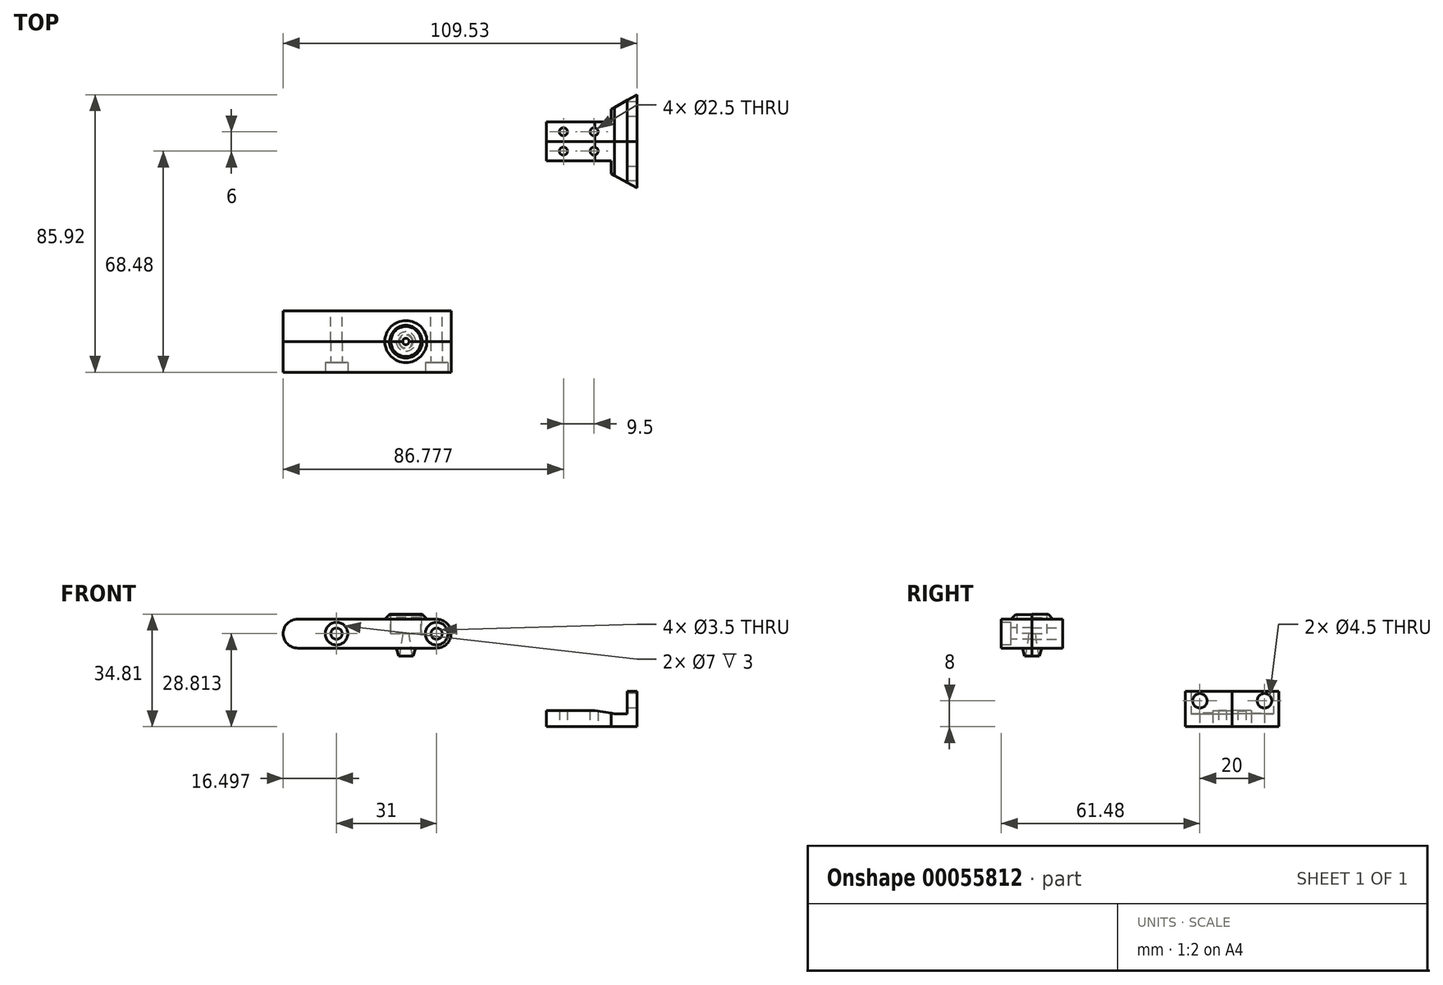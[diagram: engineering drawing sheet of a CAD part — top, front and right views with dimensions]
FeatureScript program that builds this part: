
annotation { "Feature Type Name" : "Feature", "Feature Type Description" : "" }
export const myFeature = defineFeature(function(context is Context, id is Id, definition is map)
    precondition{}
    {
        {
            var Q0;
            Q0=qCreatedBy(makeId("Front.planeOp"),FACE);
            var sketch = newSketch(context, id + "F0", { "sketchPlane" : qUnion([Q0])});
            skLineSegment(sketch, "E0.bottom", {"start": v(-22.8, 33.31) * mm, "end": v(29.2, 33.31) * mm});
            skLineSegment(sketch, "E0.top", {"start": v(-22.8, 24.31) * mm, "end": v(29.2, 24.31) * mm});
            skLineSegment(sketch, "E0.left", {"start": v(-22.8, 33.31) * mm, "end": v(-22.8, 24.31) * mm});
            skLineSegment(sketch, "E0.right", {"start": v(29.2, 33.31) * mm, "end": v(29.2, 24.31) * mm});
            skSolve(sketch);
        }
        {
            var Q0;
            Q0=makeQuery(id+"F0.imprint","IMPRINT",FACE,{"disambiguationData":[TD([[makeQuery(id+"F0.imprint","IMPRINT",EDGE,{"derivedFrom":sQuery(id+"F0.wireOp",EDGE,"E0.bottom")}),-1.0]])]});
            extrude(context, id + "F1", {"entities" : qUnion([Q0]), "depth" : 9.5 * mm});
        }
        {
            var Q0;
            Q0=makeQuery(id+"F1.opExtrude","SWEPT_FACE",FACE,{"disambiguationData":[OSD([sQuery(id+"F0.wireOp",EDGE,"E0.bottom")])]});
            var sketch = newSketch(context, id + "F2", { "sketchPlane" : qUnion([Q0])});
            skCircle(sketch, "E1", {"center": v(15.2, -9.5) * mm, "radius": 4.65 * mm});
            skCircle(sketch, "E2", {"center": v(15.2, -9.5) * mm, "radius": 6.5 * mm});
            skSolve(sketch);
        }
        {
            var Q0;
            {var subQ0=sQuery(id+"F2.wireOp",EDGE,"E1");var subQ1=makeQuery(id+"F1.opExtrude","CAP_EDGE",EDGE,{"disambiguationData":[OSD([sQuery(id+"F0.wireOp",EDGE,"E0.bottom")])],"isStart":false});var subQ2=makeQuery(id+"F2.imprint","INTERSECT",VERTEX,{"disambiguationData":[OD(0.0)],"derivedFrom":[subQ1,subQ0]});Q0=makeQuery(id+"F2.imprint","IMPRINT",FACE,{"disambiguationData":[TD([[makeQuery(id+"F2.imprint","IMPRINT",EDGE,{"disambiguationData":[TD([[subQ2,1.0]])],"derivedFrom":subQ0}),1.0]])]});}
            extrude(context, id + "F3", {"entities" : qUnion([Q0]), "operationType" : NewBodyOperationType.REMOVE, "oppositeDirection" : true, "depth" : 4.5 * mm});
        }
        {
            var Q0;
            {var subQ0=sQuery(id+"F2.wireOp",EDGE,"E1");var subQ1=makeQuery(id+"F1.opExtrude","CAP_EDGE",EDGE,{"disambiguationData":[OSD([sQuery(id+"F0.wireOp",EDGE,"E0.bottom")])],"isStart":false});var subQ2=makeQuery(id+"F2.imprint","INTERSECT",VERTEX,{"disambiguationData":[OD(0.0)],"derivedFrom":[subQ1,subQ0]});Q0=makeQuery(id+"F2.imprint","IMPRINT",FACE,{"disambiguationData":[TD([[makeQuery(id+"F2.imprint","IMPRINT",EDGE,{"disambiguationData":[TD([[subQ2,1.0]])],"derivedFrom":subQ0}),-1.0]])]});}
            var Q1;
            Q1=sQuery(id+"F2.wireOp",EDGE,"E1");
            var Q2;
            Q2=sQuery(id+"F2.wireOp",EDGE,"E2");
            extrude(context, id + "F4", {"entities" : qUnion([Q0]), "operationType" : NewBodyOperationType.ADD, "surfaceEntities" : qUnion([Q1, Q2]), "depth" : 1.5 * mm});
        }
        {
            var Q0;
            Q0=makeQuery(id+"F4.opExtrude","CAP_EDGE",EDGE,{"disambiguationData":[OSD([sQuery(id+"F2.wireOp",EDGE,"E2")])],"isStart":false});
            chamfer(context, id + "F5", {"entities" : qUnion([Q0]), "width" : 1.5 * mm});
        }
        {
            var Q0;
            {var subQ0=sQuery(id+"F2.wireOp",EDGE,"E2");var subQ1=sQuery(id+"F0.wireOp",EDGE,"E0.bottom");var subQ2=makeQuery(id+"F1.opExtrude","CAP_EDGE",EDGE,{"disambiguationData":[OSD([subQ1])],"isStart":false});Q0=makeQuery(id+"F4.boolean.opBoolean","MERGE",FACE,{"derivedFrom":[makeQuery(id+"F1.opExtrude","CAP_FACE",FACE,{"disambiguationData":[OSD([subQ1,sQuery(id+"F0.wireOp",EDGE,"E0.top"),sQuery(id+"F0.wireOp",EDGE,"E0.left"),sQuery(id+"F0.wireOp",EDGE,"E0.right")])],"isStart":false}),makeQuery(id+"F4.opExtrude","SWEPT_FACE",FACE,{"disambiguationData":[OSD([subQ1]),TDD([makeQuery(id+"F2.imprint","IMPRINT",EDGE,{"disambiguationData":[TD([[makeQuery(id+"F2.imprint","INTERSECT",VERTEX,{"disambiguationData":[OD(0.0)],"derivedFrom":[subQ2,subQ0]}),-1.0]])],"derivedFrom":subQ2})])]}),makeQuery(id+"F4.opExtrude","SWEPT_FACE",FACE,{"disambiguationData":[OSD([subQ1]),TDD([makeQuery(id+"F2.imprint","IMPRINT",EDGE,{"disambiguationData":[TD([[makeQuery(id+"F2.imprint","INTERSECT",VERTEX,{"disambiguationData":[OD(1.0)],"derivedFrom":[subQ2,subQ0]}),1.0]])],"derivedFrom":subQ2})])]})]});}
            var sketch = newSketch(context, id + "F6", { "sketchPlane" : qUnion([Q0])});
            skLineSegment(sketch, "E3", {"start": v(15.2, 28.81) * mm, "end": v(15.2, 21.81) * mm});
            skLineSegment(sketch, "E4", {"start": v(15.2, 21.81) * mm, "end": v(18.2, 21.81) * mm});
            skLineSegment(sketch, "E5", {"start": v(18.2, 21.81) * mm, "end": v(18.2, 24.31) * mm});
            skLineSegment(sketch, "E6", {"start": v(18.2, 24.31) * mm, "end": v(16.2, 28.81) * mm});
            skLineSegment(sketch, "E7", {"start": v(16.2, 28.81) * mm, "end": v(15.2, 28.81) * mm});
            skSolve(sketch);
        }
        {
            var Q0;
            {var subQ0=sQuery(id+"F6.wireOp",EDGE,"E4");Q0=makeQuery(id+"F6.imprint","IMPRINT",FACE,{"disambiguationData":[TD([[makeQuery(id+"F6.imprint","IMPRINT",EDGE,{"derivedFrom":subQ0}),1.0]])]});}
            var Q1;
            {var subQ4=sQuery(id+"F6.wireOp",EDGE,"E6");Q1=makeQuery(id+"F6.imprint","IMPRINT",FACE,{"disambiguationData":[TD([[makeQuery(id+"F6.imprint","IMPRINT",EDGE,{"derivedFrom":subQ4}),1.0]])]});}
            var Q2;
            Q2=sQuery(id+"F6.wireOp",EDGE,"E3");
            revolve(context, id + "F7", {"operationType" : NewBodyOperationType.ADD, "entities" : qUnion([Q0, Q1]), "axis" : qUnion([Q2]), "revolveType" : RevolveType.ONE_DIRECTION, "oppositeDirection" : true, "angle" : 180 * degree});
        }
        {
            var Q0;
            {var subQ0=sQuery(id+"F2.wireOp",EDGE,"E2");var subQ1=sQuery(id+"F0.wireOp",EDGE,"E0.bottom");var subQ2=makeQuery(id+"F1.opExtrude","CAP_EDGE",EDGE,{"disambiguationData":[OSD([subQ1])],"isStart":false});Q0=makeQuery(id+"F7.boolean.opBoolean","MERGE",FACE,{"derivedFrom":[makeQuery(id+"F4.boolean.opBoolean","MERGE",FACE,{"derivedFrom":[makeQuery(id+"F1.opExtrude","CAP_FACE",FACE,{"disambiguationData":[OSD([subQ1,sQuery(id+"F0.wireOp",EDGE,"E0.top"),sQuery(id+"F0.wireOp",EDGE,"E0.left"),sQuery(id+"F0.wireOp",EDGE,"E0.right")])],"isStart":false}),makeQuery(id+"F4.opExtrude","SWEPT_FACE",FACE,{"disambiguationData":[OSD([subQ1]),TDD([makeQuery(id+"F2.imprint","IMPRINT",EDGE,{"disambiguationData":[TD([[makeQuery(id+"F2.imprint","INTERSECT",VERTEX,{"disambiguationData":[OD(0.0)],"derivedFrom":[subQ2,subQ0]}),-1.0]])],"derivedFrom":subQ2})])]}),makeQuery(id+"F4.opExtrude","SWEPT_FACE",FACE,{"disambiguationData":[OSD([subQ1]),TDD([makeQuery(id+"F2.imprint","IMPRINT",EDGE,{"disambiguationData":[TD([[makeQuery(id+"F2.imprint","INTERSECT",VERTEX,{"disambiguationData":[OD(1.0)],"derivedFrom":[subQ2,subQ0]}),1.0]])],"derivedFrom":subQ2})])]})]}),makeQuery(id+"F7.opRevolve","CAP_FACE",FACE,{"disambiguationData":[OSD([sQuery(id+"F6.wireOp",EDGE,"E3"),sQuery(id+"F6.wireOp",EDGE,"E4"),sQuery(id+"F6.wireOp",EDGE,"E5"),sQuery(id+"F6.wireOp",EDGE,"E6"),sQuery(id+"F6.wireOp",EDGE,"E7")])],"isStart":false})]});}
            var sketch = newSketch(context, id + "F8", { "sketchPlane" : qUnion([Q0])});
            skLineSegment(sketch, "E8", {"start": v(15.2, 28.81) * mm, "end": v(15.2, 21.81) * mm});
            skLineSegment(sketch, "E9", {"start": v(15.2, 21.81) * mm, "end": v(17.2, 21.81) * mm});
            skLineSegment(sketch, "E10", {"start": v(17.2, 21.81) * mm, "end": v(16.2, 28.81) * mm});
            skLineSegment(sketch, "E11", {"start": v(16.2, 28.81) * mm, "end": v(15.2, 28.81) * mm});
            skSolve(sketch);
        }
        {
            var Q0;
            Q0=makeQuery(id+"F8.imprint","IMPRINT",FACE,{"disambiguationData":[TD([[makeQuery(id+"F8.imprint","IMPRINT",EDGE,{"derivedFrom":sQuery(id+"F8.wireOp",EDGE,"E8")}),1.0]])]});
            var Q1;
            Q1=sQuery(id+"F8.wireOp",EDGE,"E8");
            revolve(context, id + "F9", {"operationType" : NewBodyOperationType.REMOVE, "entities" : qUnion([Q0]), "axis" : qUnion([Q1]), "revolveType" : RevolveType.FULL, "oppositeDirection" : true});
        }
        {
            var Q0;
            Q0=makeQuery(id+"F7.opRevolve","SWEPT_EDGE",EDGE,{"disambiguationData":[OSD([sQuery(id+"F6.wireOp",EDGE,"E4"),sQuery(id+"F6.wireOp",EDGE,"E5")])]});
            chamfer(context, id + "F10", {"entities" : qUnion([Q0]), "chamferType" : ChamferType.TWO_OFFSETS, "width1" : 0.75 * mm, "oppositeDirection" : false, "width2" : 2.5 * mm, "tangentPropagation" : true});
        }
        {
            var Q0;
            Q0=qCreatedBy(makeId("Front.planeOp"),FACE);
            var sketch = newSketch(context, id + "F11", { "sketchPlane" : qUnion([Q0])});
            skCircle(sketch, "E12", {"center": v(-6.3, 28.81) * mm, "radius": 1.75 * mm});
            skCircle(sketch, "E13", {"center": v(24.7, 28.81) * mm, "radius": 1.75 * mm});
            skSolve(sketch);
        }
        {
            var Q0;
            Q0=makeQuery(id+"F11.imprint","IMPRINT",FACE,{"disambiguationData":[TD([[makeQuery(id+"F11.imprint","IMPRINT",EDGE,{"derivedFrom":sQuery(id+"F11.wireOp",EDGE,"E13")}),1.0]])]});
            var Q1;
            Q1=makeQuery(id+"F11.imprint","IMPRINT",FACE,{"disambiguationData":[TD([[makeQuery(id+"F11.imprint","IMPRINT",EDGE,{"derivedFrom":sQuery(id+"F11.wireOp",EDGE,"E12")}),1.0]])]});
            extrude(context, id + "F12", {"entities" : qUnion([Q0, Q1]), "operationType" : NewBodyOperationType.REMOVE, "depth" : 42.06 * mm});
        }
        {
            var Q0;
            Q0=makeQuery(id+"F1.opExtrude","SWEPT_EDGE",EDGE,{"disambiguationData":[OSD([sQuery(id+"F0.wireOp",EDGE,"E0.bottom"),sQuery(id+"F0.wireOp",EDGE,"E0.right")])]});
            var Q1;
            Q1=makeQuery(id+"F1.opExtrude","SWEPT_EDGE",EDGE,{"disambiguationData":[OSD([sQuery(id+"F0.wireOp",EDGE,"E0.top"),sQuery(id+"F0.wireOp",EDGE,"E0.right")])]});
            var Q2;
            Q2=makeQuery(id+"F1.opExtrude","SWEPT_EDGE",EDGE,{"disambiguationData":[OSD([sQuery(id+"F0.wireOp",EDGE,"E0.bottom"),sQuery(id+"F0.wireOp",EDGE,"E0.left")])]});
            var Q3;
            Q3=makeQuery(id+"F1.opExtrude","SWEPT_EDGE",EDGE,{"disambiguationData":[OSD([sQuery(id+"F0.wireOp",EDGE,"E0.top"),sQuery(id+"F0.wireOp",EDGE,"E0.left")])]});
            fillet(context, id + "F13", {"entities" : qUnion([Q0, Q1, Q2, Q3]), "radius" : 4.5 * mm, "tangentPropagation" : true, "allowEdgeOverflow" : false});
        }
        {
            var Q0;
            Q0=makeQuery(id+"F1.opExtrude","SWEPT_BODY",BODY,{"disambiguationData":[OSD([sQuery(id+"F0.wireOp",EDGE,"E0.bottom"),sQuery(id+"F0.wireOp",EDGE,"E0.top"),sQuery(id+"F0.wireOp",EDGE,"E0.left"),sQuery(id+"F0.wireOp",EDGE,"E0.right")])]});
            var Q1;
            {var subQ0=sQuery(id+"F6.wireOp",EDGE,"E4");var subQ1=sQuery(id+"F2.wireOp",EDGE,"E2");var subQ3=sQuery(id+"F0.wireOp",EDGE,"E0.bottom");var subQ4=sQuery(id+"F6.wireOp",EDGE,"E5");var subQ5=sQuery(id+"F0.wireOp",EDGE,"E0.top");var subQ6=sQuery(id+"F0.wireOp",EDGE,"E0.left");var subQ7=makeQuery(id+"F1.opExtrude","CAP_EDGE",EDGE,{"disambiguationData":[OSD([subQ3])],"isStart":false});Q1=makeQuery(id+"F9.boolean.opBoolean","SPLIT",FACE,{"disambiguationData":[TD([makeQuery(id+"F1.opExtrude","SWEPT_FACE",FACE,{"disambiguationData":[OSD([subQ6])]})])],"derivedFrom":makeQuery(id+"F7.boolean.opBoolean","MERGE",FACE,{"derivedFrom":[makeQuery(id+"F4.boolean.opBoolean","MERGE",FACE,{"derivedFrom":[makeQuery(id+"F1.opExtrude","CAP_FACE",FACE,{"disambiguationData":[OSD([subQ3,subQ5,subQ6,sQuery(id+"F0.wireOp",EDGE,"E0.right")])],"isStart":false}),makeQuery(id+"F4.opExtrude","SWEPT_FACE",FACE,{"disambiguationData":[OSD([subQ3]),TDD([makeQuery(id+"F2.imprint","IMPRINT",EDGE,{"disambiguationData":[TD([[makeQuery(id+"F2.imprint","INTERSECT",VERTEX,{"disambiguationData":[OD(0.0)],"derivedFrom":[subQ7,subQ1]}),-1.0]])],"derivedFrom":subQ7})])]}),makeQuery(id+"F4.opExtrude","SWEPT_FACE",FACE,{"disambiguationData":[OSD([subQ3]),TDD([makeQuery(id+"F2.imprint","IMPRINT",EDGE,{"disambiguationData":[TD([[makeQuery(id+"F2.imprint","INTERSECT",VERTEX,{"disambiguationData":[OD(1.0)],"derivedFrom":[subQ7,subQ1]}),1.0]])],"derivedFrom":subQ7})])]})]}),makeQuery(id+"F7.opRevolve","CAP_FACE",FACE,{"disambiguationData":[OSD([sQuery(id+"F6.wireOp",EDGE,"E3"),subQ0,subQ4,sQuery(id+"F6.wireOp",EDGE,"E6"),sQuery(id+"F6.wireOp",EDGE,"E7")])],"isStart":false})]})});}
            mirror(context, id + "F14", {"entities" : qUnion([Q0]), "mirrorPlane" : qUnion([Q1])});
        }
        {
            var Q0;
            Q0=makeQuery(id+"F14.opPattern","COPY",FACE,{"derivedFrom":makeQuery(id+"F1.opExtrude","CAP_FACE",FACE,{"disambiguationData":[OSD([sQuery(id+"F0.wireOp",EDGE,"E0.bottom"),sQuery(id+"F0.wireOp",EDGE,"E0.top"),sQuery(id+"F0.wireOp",EDGE,"E0.left"),sQuery(id+"F0.wireOp",EDGE,"E0.right")])],"isStart":true}),"instanceName":"1"});
            var sketch = newSketch(context, id + "F15", { "sketchPlane" : qUnion([Q0])});
            skCircle(sketch, "E14", {"center": v(-6.3, 28.81) * mm, "radius": 3.5 * mm});
            skCircle(sketch, "E15", {"center": v(24.7, 28.81) * mm, "radius": 3.5 * mm});
            skSolve(sketch);
        }
        {
            var Q0;
            Q0=makeQuery(id+"F15.imprint","IMPRINT",FACE,{"disambiguationData":[TD([[makeQuery(id+"F15.imprint","IMPRINT",EDGE,{"derivedFrom":sQuery(id+"F15.wireOp",EDGE,"E14")}),1.0]])]});
            var Q1;
            Q1=makeQuery(id+"F15.imprint","IMPRINT",FACE,{"disambiguationData":[TD([[makeQuery(id+"F15.imprint","IMPRINT",EDGE,{"derivedFrom":sQuery(id+"F15.wireOp",EDGE,"E15")}),1.0]])]});
            extrude(context, id + "F16", {"entities" : qUnion([Q0, Q1]), "operationType" : NewBodyOperationType.REMOVE, "oppositeDirection" : true, "depth" : 3 * mm});
        }
        {
            var Q0;
            Q0=qCreatedBy(makeId("Top.planeOp"),FACE);
            var sketch = newSketch(context, id + "F17", { "sketchPlane" : qUnion([Q0])});
            skLineSegment(sketch, "E16.bottom", {"start": v(58.73, 58.48) * mm, "end": v(78.73, 58.48) * mm});
            skLineSegment(sketch, "E16.top", {"start": v(58.73, 52.48) * mm, "end": v(78.73, 52.48) * mm});
            skLineSegment(sketch, "E16.left", {"start": v(58.73, 58.48) * mm, "end": v(58.73, 52.48) * mm});
            skLineSegment(sketch, "E16.right", {"start": v(78.73, 58.48) * mm, "end": v(78.73, 52.48) * mm});
            skCircle(sketch, "E17", {"center": v(63.98, 55.48) * mm, "radius": 1.25 * mm});
            skCircle(sketch, "E18", {"center": v(73.48, 55.48) * mm, "radius": 1.25 * mm});
            skSolve(sketch);
        }
        {
            var Q0;
            Q0=makeQuery(id+"F17.imprint","IMPRINT",FACE,{"disambiguationData":[TD([[makeQuery(id+"F17.imprint","IMPRINT",EDGE,{"derivedFrom":sQuery(id+"F17.wireOp",EDGE,"E16.bottom")}),-1.0]])]});
            extrude(context, id + "F18", {"entities" : qUnion([Q0]), "depth" : 5 * mm});
        }
        {
            var Q0;
            Q0=makeQuery(id+"F18.opExtrude","SWEPT_FACE",FACE,{"disambiguationData":[OSD([sQuery(id+"F17.wireOp",EDGE,"E16.top")])]});
            var sketch = newSketch(context, id + "F19", { "sketchPlane" : qUnion([Q0])});
            skLineSegment(sketch, "E19", {"start": v(78.73, 5) * mm, "end": v(83.73, 5) * mm});
            skLineSegment(sketch, "E20", {"start": v(83.73, 5) * mm, "end": v(83.73, 11) * mm});
            skLineSegment(sketch, "E21", {"start": v(83.73, 11) * mm, "end": v(86.73, 11) * mm});
            skLineSegment(sketch, "E22", {"start": v(86.73, 11) * mm, "end": v(86.73, 0) * mm});
            skLineSegment(sketch, "E23", {"start": v(86.73, 0) * mm, "end": v(78.73, 0) * mm});
            skSolve(sketch);
        }
        {
            var Q0;
            Q0=makeQuery(id+"F19.imprint","IMPRINT",FACE,{"disambiguationData":[TD([[makeQuery(id+"F19.imprint","IMPRINT",EDGE,{"derivedFrom":sQuery(id+"F19.wireOp",EDGE,"E19")}),-1.0]])]});
            extrude(context, id + "F20", {"entities" : qUnion([Q0]), "operationType" : NewBodyOperationType.ADD, "oppositeDirection" : true, "depth" : 15 * mm});
        }
        {
            var Q0;
            Q0=makeQuery(id+"F20.opExtrude","CAP_EDGE",EDGE,{"disambiguationData":[OSD([sQuery(id+"F17.wireOp",EDGE,"E16.top"),sQuery(id+"F17.wireOp",EDGE,"E16.right")])],"isStart":false});
            chamfer(context, id + "F21", {"entities" : qUnion([Q0]), "chamferType" : ChamferType.TWO_OFFSETS, "width1" : 9 * mm, "oppositeDirection" : false, "width2" : 5 * mm, "tangentPropagation" : true});
        }
        {
            var Q0;
            Q0=makeQuery(id+"F20.opExtrude","SWEPT_FACE",FACE,{"disambiguationData":[OSD([sQuery(id+"F19.wireOp",EDGE,"E20")])]});
            var sketch = newSketch(context, id + "F22", { "sketchPlane" : qUnion([Q0])});
            skCircle(sketch, "E24", {"center": v(-62.48, 8) * mm, "radius": 2.25 * mm});
            skPoint(sketch, "E24.centerSnap0", {"position": v(-62.48, 11) * mm});
            skPoint(sketch, "E24.centerSnap1", {"position": v(-54.98, 8) * mm});
            skSolve(sketch);
        }
        {
            var Q0;
            Q0=makeQuery(id+"F22.imprint","IMPRINT",FACE,{"disambiguationData":[TD([[makeQuery(id+"F22.imprint","IMPRINT",EDGE,{"derivedFrom":sQuery(id+"F22.wireOp",EDGE,"E24")}),1.0]])]});
            extrude(context, id + "F23", {"entities" : qUnion([Q0]), "operationType" : NewBodyOperationType.REMOVE, "oppositeDirection" : true, "depth" : 25 * mm});
        }
        {
            var Q0;
            {var subQ0=sQuery(id+"F17.wireOp",EDGE,"E16.top");Q0=makeQuery(id+"F20.boolean.opBoolean","MERGE",FACE,{"derivedFrom":[makeQuery(id+"F18.opExtrude","SWEPT_FACE",FACE,{"disambiguationData":[OSD([subQ0])]}),makeQuery(id+"F20.opExtrude","CAP_FACE",FACE,{"disambiguationData":[OSD([subQ0,sQuery(id+"F17.wireOp",EDGE,"E16.right"),sQuery(id+"F19.wireOp",EDGE,"E19"),sQuery(id+"F19.wireOp",EDGE,"E20"),sQuery(id+"F19.wireOp",EDGE,"E21"),sQuery(id+"F19.wireOp",EDGE,"E22"),sQuery(id+"F19.wireOp",EDGE,"E23")])],"isStart":true})]});}
            var sketch = newSketch(context, id + "F24", { "sketchPlane" : qUnion([Q0])});
            skLineSegment(sketch, "E25", {"start": v(83.73, 5) * mm, "end": v(83.73, 4) * mm});
            skLineSegment(sketch, "E26", {"start": v(83.73, 4) * mm, "end": v(79.73, 4) * mm});
            skLineSegment(sketch, "E27", {"start": v(79.73, 4) * mm, "end": v(73.73, 5) * mm});
            skSolve(sketch);
        }
        {
            var Q0;
            {var subQ0=sQuery(id+"F24.wireOp",EDGE,"E25");Q0=makeQuery(id+"F24.imprint","IMPRINT",FACE,{"disambiguationData":[TD([[makeQuery(id+"F24.imprint","IMPRINT",EDGE,{"derivedFrom":subQ0}),-1.0]])]});}
            extrude(context, id + "F25", {"entities" : qUnion([Q0]), "operationType" : NewBodyOperationType.REMOVE, "oppositeDirection" : true, "depth" : 25 * mm});
        }
        {
            var Q0;
            Q0=makeQuery(id+"F18.opExtrude","SWEPT_BODY",BODY,{"disambiguationData":[OSD([sQuery(id+"F17.wireOp",EDGE,"E16.bottom"),sQuery(id+"F17.wireOp",EDGE,"E16.top"),sQuery(id+"F17.wireOp",EDGE,"E16.left"),sQuery(id+"F17.wireOp",EDGE,"E16.right"),sQuery(id+"F17.wireOp",EDGE,"E17"),sQuery(id+"F17.wireOp",EDGE,"E18")])]});
            var Q1;
            {var subQ0=sQuery(id+"F17.wireOp",EDGE,"E16.top");Q1=makeQuery(id+"F20.boolean.opBoolean","MERGE",FACE,{"derivedFrom":[makeQuery(id+"F18.opExtrude","SWEPT_FACE",FACE,{"disambiguationData":[OSD([subQ0])]}),makeQuery(id+"F20.opExtrude","CAP_FACE",FACE,{"disambiguationData":[OSD([subQ0,sQuery(id+"F17.wireOp",EDGE,"E16.right"),sQuery(id+"F19.wireOp",EDGE,"E19"),sQuery(id+"F19.wireOp",EDGE,"E20"),sQuery(id+"F19.wireOp",EDGE,"E21"),sQuery(id+"F19.wireOp",EDGE,"E22"),sQuery(id+"F19.wireOp",EDGE,"E23")])],"isStart":true})]});}
            mirror(context, id + "F26", {"entities" : qUnion([Q0]), "mirrorPlane" : qUnion([Q1])});
        }
        {
            var Q0;
            {var subQ0=sQuery(id+"F2.wireOp",EDGE,"E1");var subQ1=sQuery(id+"F0.wireOp",EDGE,"E0.bottom");var subQ2=makeQuery(id+"F2.imprint","INTERSECT",VERTEX,{"disambiguationData":[OD(0.0)],"derivedFrom":[makeQuery(id+"F1.opExtrude","CAP_EDGE",EDGE,{"disambiguationData":[OSD([subQ1])],"isStart":false}),subQ0]});Q0=makeQuery(id+"F14.opPattern","COPY",EDGE,{"derivedFrom":makeQuery(id+"F4.boolean.opBoolean","MERGE",EDGE,{"derivedFrom":[makeQuery(id+"F3.boolean.opBoolean","COPY",EDGE,{"derivedFrom":makeQuery(id+"F3.opExtrude","SWEPT_EDGE",EDGE,{"disambiguationData":[OSD([subQ1,subQ0]),TDD([subQ2])]})}),makeQuery(id+"F4.opExtrude","SWEPT_EDGE",EDGE,{"disambiguationData":[OSD([subQ1,subQ0]),TDD([subQ2])]})]}),"instanceName":"1"});}
            var Q1;
            {var subQ0=sQuery(id+"F2.wireOp",EDGE,"E1");var subQ1=sQuery(id+"F0.wireOp",EDGE,"E0.bottom");var subQ2=makeQuery(id+"F2.imprint","INTERSECT",VERTEX,{"disambiguationData":[OD(1.0)],"derivedFrom":[makeQuery(id+"F1.opExtrude","CAP_EDGE",EDGE,{"disambiguationData":[OSD([subQ1])],"isStart":false}),subQ0]});Q1=makeQuery(id+"F14.opPattern","COPY",EDGE,{"derivedFrom":makeQuery(id+"F4.boolean.opBoolean","MERGE",EDGE,{"derivedFrom":[makeQuery(id+"F3.boolean.opBoolean","COPY",EDGE,{"derivedFrom":makeQuery(id+"F3.opExtrude","SWEPT_EDGE",EDGE,{"disambiguationData":[OSD([subQ1,subQ0]),TDD([subQ2])]})}),makeQuery(id+"F4.opExtrude","SWEPT_EDGE",EDGE,{"disambiguationData":[OSD([subQ1,subQ0]),TDD([subQ2])]})]}),"instanceName":"1"});}
            var Q2;
            {var subQ0=sQuery(id+"F2.wireOp",EDGE,"E1");var subQ1=sQuery(id+"F0.wireOp",EDGE,"E0.bottom");var subQ2=makeQuery(id+"F2.imprint","INTERSECT",VERTEX,{"disambiguationData":[OD(0.0)],"derivedFrom":[makeQuery(id+"F1.opExtrude","CAP_EDGE",EDGE,{"disambiguationData":[OSD([subQ1])],"isStart":false}),subQ0]});Q2=makeQuery(id+"F4.boolean.opBoolean","MERGE",EDGE,{"derivedFrom":[makeQuery(id+"F3.boolean.opBoolean","COPY",EDGE,{"derivedFrom":makeQuery(id+"F3.opExtrude","SWEPT_EDGE",EDGE,{"disambiguationData":[OSD([subQ1,subQ0]),TDD([subQ2])]})}),makeQuery(id+"F4.opExtrude","SWEPT_EDGE",EDGE,{"disambiguationData":[OSD([subQ1,subQ0]),TDD([subQ2])]})]});}
            var Q3;
            {var subQ0=sQuery(id+"F2.wireOp",EDGE,"E1");var subQ1=sQuery(id+"F0.wireOp",EDGE,"E0.bottom");var subQ2=makeQuery(id+"F2.imprint","INTERSECT",VERTEX,{"disambiguationData":[OD(1.0)],"derivedFrom":[makeQuery(id+"F1.opExtrude","CAP_EDGE",EDGE,{"disambiguationData":[OSD([subQ1])],"isStart":false}),subQ0]});Q3=makeQuery(id+"F4.boolean.opBoolean","MERGE",EDGE,{"derivedFrom":[makeQuery(id+"F3.boolean.opBoolean","COPY",EDGE,{"derivedFrom":makeQuery(id+"F3.opExtrude","SWEPT_EDGE",EDGE,{"disambiguationData":[OSD([subQ1,subQ0]),TDD([subQ2])]})}),makeQuery(id+"F4.opExtrude","SWEPT_EDGE",EDGE,{"disambiguationData":[OSD([subQ1,subQ0]),TDD([subQ2])]})]});}
            chamfer(context, id + "F27", {"entities" : qUnion([Q0, Q1, Q2, Q3]), "width" : .1 * mm, "tangentPropagation" : true});
        }
        {
            var Q0;
            Q0=makeQuery(id+"F14.opPattern","COPY",EDGE,{"derivedFrom":makeQuery(id+"F4.opExtrude","CAP_EDGE",EDGE,{"disambiguationData":[OSD([sQuery(id+"F2.wireOp",EDGE,"E1")])],"isStart":false}),"instanceName":"1"});
            chamfer(context, id + "F28", {"entities" : qUnion([Q0]), "chamferType" : ChamferType.TWO_OFFSETS, "width1" : .2 * mm, "oppositeDirection" : false, "width2" : 1 * mm, "tangentPropagation" : true});
        }
        {
            var Q0;
            Q0=makeQuery(id+"F4.opExtrude","CAP_EDGE",EDGE,{"disambiguationData":[OSD([sQuery(id+"F2.wireOp",EDGE,"E1")])],"isStart":false});
            chamfer(context, id + "F29", {"entities" : qUnion([Q0]), "chamferType" : ChamferType.TWO_OFFSETS, "width1" : .2 * mm, "oppositeDirection" : true, "width2" : 1 * mm, "tangentPropagation" : true});
        }
    });
